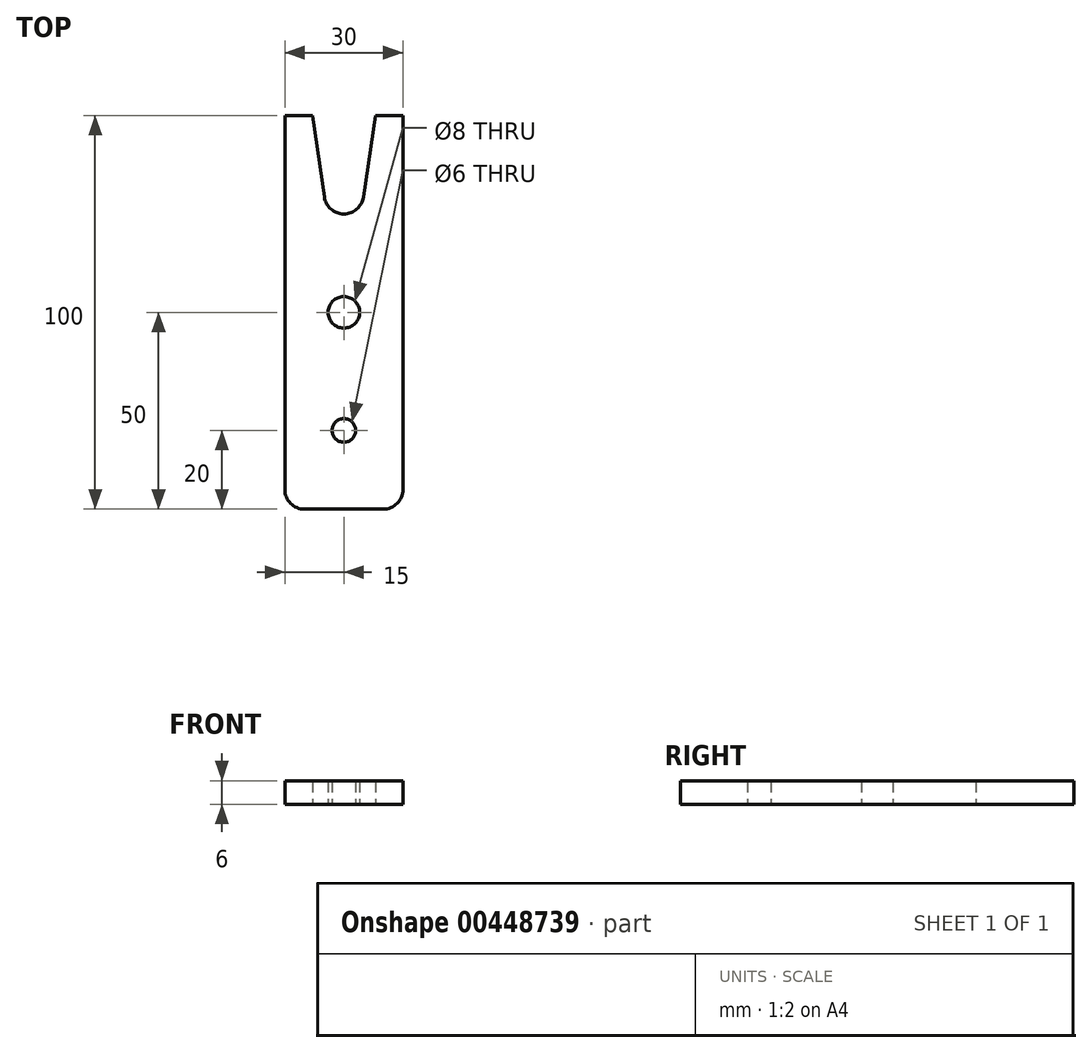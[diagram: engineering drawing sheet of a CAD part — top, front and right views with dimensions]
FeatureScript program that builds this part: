
annotation { "Feature Type Name" : "Feature", "Feature Type Description" : "" }
export const myFeature = defineFeature(function(context is Context, id is Id, definition is map)
    precondition{}
    {
        {
            var Q0;
            Q0=qCreatedBy(makeId("Top.planeOp"),FACE);
            var sketch = newSketch(context, id + "F0", { "sketchPlane" : qUnion([Q0])});
            skLineSegment(sketch, "E0.bottom", {"start": v(-15, 50) * mm, "end": v(15, 50) * mm});
            skLineSegment(sketch, "E0.top", {"start": v(-10, -50) * mm, "end": v(10, -50) * mm});
            skLineSegment(sketch, "E0.left", {"start": v(-15, 50) * mm, "end": v(-15, -45) * mm});
            skLineSegment(sketch, "E0.right", {"start": v(15, 50) * mm, "end": v(15, -45) * mm});
            skPoint(sketch, "E0.middle", {"position": v(0, 0) * mm});
            skPoint(sketch, "E1.visualSharp", {"position": v(-15, -50) * mm});
            skArc(sketch, "E1.filletArc", {"start": v(-15, -45) * mm, "mid": v(-13.54, -48.54) * mm, "end": v(-10, -50) * mm});
            skPoint(sketch, "E2.visualSharp", {"position": v(15, -50) * mm});
            skArc(sketch, "E2.filletArc", {"start": v(10, -50) * mm, "mid": v(13.54, -48.54) * mm, "end": v(15, -45) * mm});
            skLineSegment(sketch, "E3", {"start": v(0, 50) * mm, "end": v(0, 30) * mm});
            skPoint(sketch, "E3.endSnap0", {"position": v(0, 50) * mm});
            skCircle(sketch, "E4", {"center": v(0, 30) * mm, "radius": 5 * mm});
            skLineSegment(sketch, "E5", {"start": v(-15, 50) * mm, "end": v(-8, 50) * mm});
            skLineSegment(sketch, "E6", {"start": v(-8, 50) * mm, "end": v(15, 50) * mm});
            skLineSegment(sketch, "E7", {"start": v(15, 50) * mm, "end": v(8, 50) * mm});
            skLineSegment(sketch, "E8", {"start": v(0, -50) * mm, "end": v(0, -30) * mm});
            skPoint(sketch, "E8.endSnap0", {"position": v(0, -50) * mm});
            skCircle(sketch, "E9", {"center": v(0, -30) * mm, "radius": 3 * mm});
            skCircle(sketch, "E10", {"center": v(0, 0) * mm, "radius": 4 * mm});
            skLineSegment(sketch, "E11", {"start": v(8, 50) * mm, "end": v(4.95, 29.27) * mm});
            skLineSegment(sketch, "E12", {"start": v(-8, 50) * mm, "end": v(-4.95, 29.27) * mm});
            skSolve(sketch);
        }
        {
            var Q0;
            Q0=makeQuery(id+"F0.imprint","IMPRINT",FACE,{"disambiguationData":[TD([[makeQuery(id+"F0.imprint","IMPRINT",EDGE,{"derivedFrom":sQuery(id+"F0.wireOp",EDGE,"E0.left")}),1.0]])]});
            extrude(context, id + "F1", {"entities" : qUnion([Q0]), "depth" : 6 * mm});
        }
    });
